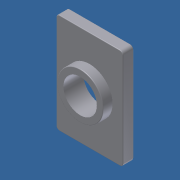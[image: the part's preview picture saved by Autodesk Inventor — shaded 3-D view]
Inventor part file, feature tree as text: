
AUTODESK INVENTOR PART (.ipt)
format: ipt  version: 2012 SP1 (Build 160190100, 190)  size: 131,072 bytes
history: native  units: in
note: dims shown in document units (in); Inventor stores cm internally (conversion verified against a paired STEP export)
features: extrude x3, sketch x3, fillet x2
ambient origin geometry x8: Origin, YZ Plane, XZ Plane, XY Plane, X Axis, Y Axis, Z Axis, Center Point
bodies: Solid1 (feature_tree)
feature tree (8):
  extrude  "Extrusion1"  Depth=0.5906in
  extrude  "Extrusion2"  Depth=0.2717in
  extrude  "Extrusion3"  Depth=0.2953in
  fillet  "Fillet1"  Radius=0.0551in
  fillet  "Fillet2"  Radius=0.1969in
  sketch  "Sketch1"  dims[d0=0.3937in d1=0.5906in]
  sketch  "Sketch2"  dims[d2=0.063in d3=0.0in d4=0.2717in]
  sketch  "Sketch3"  dims[d5=0.1969in d6=0.2953in d7=0.0551in d8=0.0in d9=0.1969in d10=0.0551in d11=0.0in d12=0.0197in d13=0.0039in]
